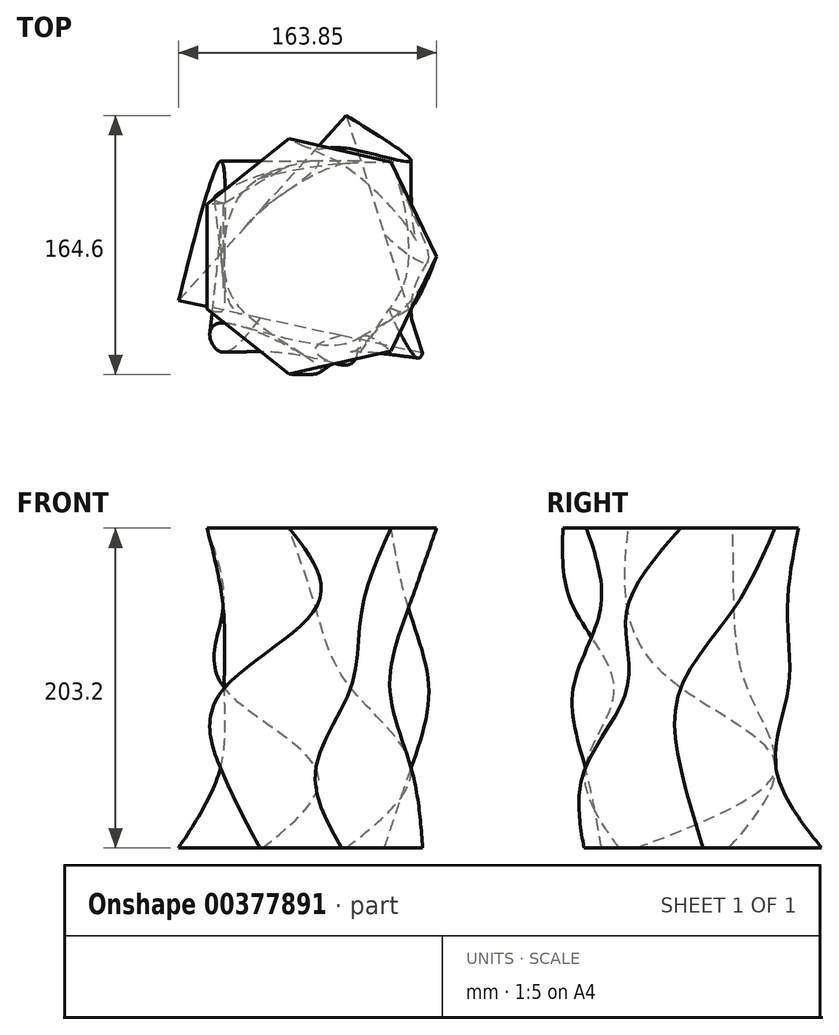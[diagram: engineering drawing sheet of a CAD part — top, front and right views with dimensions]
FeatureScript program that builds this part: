
annotation { "Feature Type Name" : "Feature", "Feature Type Description" : "" }
export const myFeature = defineFeature(function(context is Context, id is Id, definition is map)
    precondition{}
    {
        {
            var Q0;
            Q0=qCreatedBy(makeId("Top.planeOp"),FACE);
            cPlane(context, id + "F0", {"entities" : qUnion([Q0]), "cplaneType" : CPlaneType.OFFSET, "offset" : 50.8 * mm, "width" : 152.4 * mm, "height" : 152.4 * mm});
        }
        {
            var Q0;
            Q0=qCreatedBy(id+"F0.planeOp",FACE);
            cPlane(context, id + "F1", {"entities" : qUnion([Q0]), "cplaneType" : CPlaneType.OFFSET, "offset" : 50.8 * mm, "width" : 152.4 * mm, "height" : 152.4 * mm});
        }
        {
            var Q0;
            Q0=qCreatedBy(id+"F1.planeOp",FACE);
            cPlane(context, id + "F2", {"entities" : qUnion([Q0]), "cplaneType" : CPlaneType.OFFSET, "offset" : 50.8 * mm, "width" : 152.4 * mm, "height" : 152.4 * mm});
        }
        {
            var Q0;
            Q0=qCreatedBy(id+"F2.planeOp",FACE);
            cPlane(context, id + "F3", {"entities" : qUnion([Q0]), "cplaneType" : CPlaneType.OFFSET, "offset" : 50.8 * mm, "width" : 152.4 * mm, "height" : 152.4 * mm});
        }
        {
            var Q0;
            Q0=qCreatedBy(makeId("Top.planeOp"),FACE);
            var sketch = newSketch(context, id + "F4", { "sketchPlane" : qUnion([Q0])});
            skCircle(sketch, "E0.cCircle", {"center": v(0, 0) * mm, "radius": 45.78 * mm, "construction": true});
            skLineSegment(sketch, "E0.0", {"start": v(19.28, 89.51) * mm, "end": v(67.88, -61.46) * mm});
            skLineSegment(sketch, "E0.1", {"start": v(67.88, -61.46) * mm, "end": v(-87.16, -28.06) * mm});
            skLineSegment(sketch, "E0.2", {"start": v(-87.16, -28.06) * mm, "end": v(19.28, 89.51) * mm});
            skPoint(sketch, "E0.0.midPoint", {"position": v(43.58, 14.03) * mm});
            skSolve(sketch);
        }
        {
            var Q0;
            Q0=qCreatedBy(id+"F0.planeOp",FACE);
            var sketch = newSketch(context, id + "F5", { "sketchPlane" : qUnion([Q0])});
            skCircle(sketch, "E1.cCircle", {"center": v(0, 0) * mm, "radius": 60.55 * mm, "construction": true});
            skLineSegment(sketch, "E1.0", {"start": v(-60.55, 60.55) * mm, "end": v(-60.55, -60.55) * mm});
            skLineSegment(sketch, "E1.1", {"start": v(60.55, 60.55) * mm, "end": v(-60.55, 60.55) * mm});
            skLineSegment(sketch, "E1.2", {"start": v(60.55, -60.55) * mm, "end": v(60.55, 60.55) * mm});
            skLineSegment(sketch, "E1.3", {"start": v(-60.55, -60.55) * mm, "end": v(60.55, -60.55) * mm});
            skPoint(sketch, "E1.0.midPoint", {"position": v(-60.55, 0) * mm});
            skSolve(sketch);
        }
        {
            var Q0;
            Q0=qCreatedBy(id+"F1.planeOp",FACE);
            var sketch = newSketch(context, id + "F6", { "sketchPlane" : qUnion([Q0])});
            skCircle(sketch, "E2.cCircle", {"center": v(0, 0) * mm, "radius": 58.08 * mm, "construction": true});
            skLineSegment(sketch, "E2.0", {"start": v(-58.08, 42.2) * mm, "end": v(-58.08, -42.2) * mm});
            skLineSegment(sketch, "E2.1", {"start": v(22.19, 68.28) * mm, "end": v(-58.08, 42.2) * mm});
            skLineSegment(sketch, "E2.2", {"start": v(71.8, 0) * mm, "end": v(22.19, 68.28) * mm});
            skLineSegment(sketch, "E2.3", {"start": v(22.19, -68.28) * mm, "end": v(71.8, 0) * mm});
            skLineSegment(sketch, "E2.4", {"start": v(-58.08, -42.2) * mm, "end": v(22.19, -68.28) * mm});
            skPoint(sketch, "E2.0.midPoint", {"position": v(-58.08, 0) * mm});
            skSolve(sketch);
        }
        {
            var Q0;
            Q0=qCreatedBy(id+"F2.planeOp",FACE);
            var sketch = newSketch(context, id + "F7", { "sketchPlane" : qUnion([Q0])});
            skCircle(sketch, "E3.cCircle", {"center": v(0, 0) * mm, "radius": 58.78 * mm, "construction": true});
            skLineSegment(sketch, "E3.0", {"start": v(58.78, 33.93) * mm, "end": v(58.78, -33.93) * mm});
            skLineSegment(sketch, "E3.1", {"start": v(58.78, -33.93) * mm, "end": v(0, -67.87) * mm});
            skLineSegment(sketch, "E3.2", {"start": v(0, -67.87) * mm, "end": v(-58.78, -33.93) * mm});
            skLineSegment(sketch, "E3.3", {"start": v(-58.78, -33.93) * mm, "end": v(-58.78, 33.93) * mm});
            skLineSegment(sketch, "E3.4", {"start": v(-58.78, 33.93) * mm, "end": v(0, 67.87) * mm});
            skLineSegment(sketch, "E3.5", {"start": v(0, 67.87) * mm, "end": v(58.78, 33.93) * mm});
            skPoint(sketch, "E3.0.midPoint", {"position": v(58.78, 0) * mm});
            skSolve(sketch);
        }
        {
            var Q0;
            Q0=qCreatedBy(id+"F3.planeOp",FACE);
            var sketch = newSketch(context, id + "F8", { "sketchPlane" : qUnion([Q0])});
            skCircle(sketch, "E4.cCircle", {"center": v(0, 0) * mm, "radius": 69.1 * mm, "construction": true});
            skLineSegment(sketch, "E4.0", {"start": v(76.7, 0) * mm, "end": v(47.82, -59.96) * mm});
            skLineSegment(sketch, "E4.1", {"start": v(47.82, -59.96) * mm, "end": v(-17.07, -74.77) * mm});
            skLineSegment(sketch, "E4.2", {"start": v(-17.07, -74.77) * mm, "end": v(-69.1, -33.28) * mm});
            skLineSegment(sketch, "E4.3", {"start": v(-69.1, -33.28) * mm, "end": v(-69.1, 33.28) * mm});
            skLineSegment(sketch, "E4.4", {"start": v(-69.1, 33.28) * mm, "end": v(-17.07, 74.77) * mm});
            skLineSegment(sketch, "E4.5", {"start": v(-17.07, 74.77) * mm, "end": v(47.82, 59.96) * mm});
            skLineSegment(sketch, "E4.6", {"start": v(47.82, 59.96) * mm, "end": v(76.7, 0) * mm});
            skPoint(sketch, "E4.0.midPoint", {"position": v(62.26, -29.98) * mm});
            skSolve(sketch);
        }
        {
            var Q0;
            Q0=makeQuery(id+"F4.imprint","IMPRINT",FACE,{"disambiguationData":[TD([[makeQuery(id+"F4.imprint","IMPRINT",EDGE,{"derivedFrom":sQuery(id+"F4.wireOp",EDGE,"E0.0")}),-1.0]])]});
            var Q1;
            Q1=makeQuery(id+"F5.imprint","IMPRINT",FACE,{"disambiguationData":[TD([[makeQuery(id+"F5.imprint","IMPRINT",EDGE,{"derivedFrom":sQuery(id+"F5.wireOp",EDGE,"E1.0")}),1.0]])]});
            var Q2;
            Q2=makeQuery(id+"F6.imprint","IMPRINT",FACE,{"disambiguationData":[TD([[makeQuery(id+"F6.imprint","IMPRINT",EDGE,{"derivedFrom":sQuery(id+"F6.wireOp",EDGE,"E2.0")}),1.0]])]});
            var Q3;
            Q3=makeQuery(id+"F7.imprint","IMPRINT",FACE,{"disambiguationData":[TD([[makeQuery(id+"F7.imprint","IMPRINT",EDGE,{"derivedFrom":sQuery(id+"F7.wireOp",EDGE,"E3.0")}),-1.0]])]});
            var Q4;
            Q4=makeQuery(id+"F8.imprint","IMPRINT",FACE,{"disambiguationData":[TD([[makeQuery(id+"F8.imprint","IMPRINT",EDGE,{"derivedFrom":sQuery(id+"F8.wireOp",EDGE,"E4.0")}),-1.0]])]});
            loft(context, id + "F9", {"sheetProfilesArray" : [{ "sheetProfileEntities" : qUnion([Q0]) }, { "sheetProfileEntities" : qUnion([Q1]) }, { "sheetProfileEntities" : qUnion([Q2]) }, { "sheetProfileEntities" : qUnion([Q3]) }, { "sheetProfileEntities" : qUnion([Q4]) }]});
        }
    });
